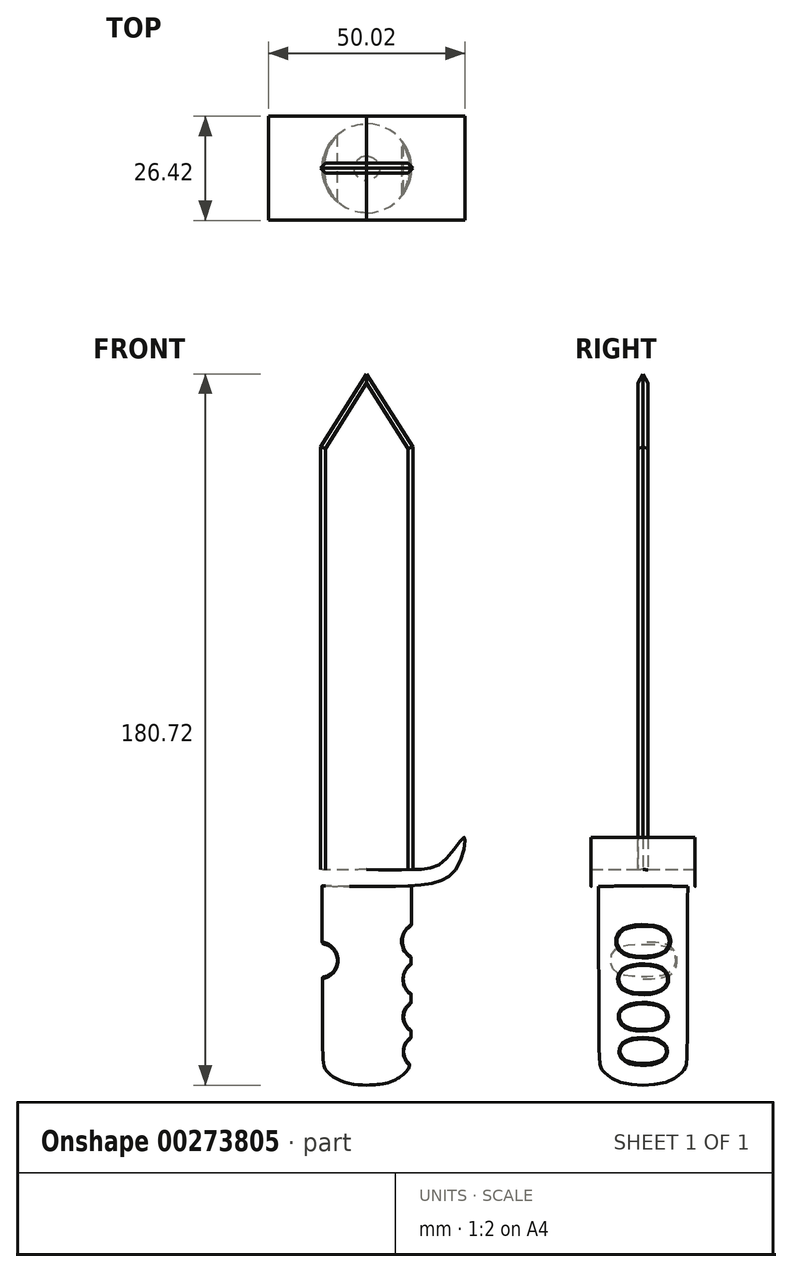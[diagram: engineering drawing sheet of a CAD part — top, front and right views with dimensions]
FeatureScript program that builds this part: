
annotation { "Feature Type Name" : "Feature", "Feature Type Description" : "" }
export const myFeature = defineFeature(function(context is Context, id is Id, definition is map)
    precondition{}
    {
        {
            var Q0;
            Q0=qCreatedBy(makeId("Front.planeOp"),FACE);
            var sketch = newSketch(context, id + "F0", { "sketchPlane" : qUnion([Q0])});
            skLineSegment(sketch, "E0", {"start": v(-11.8, -23.78) * mm, "end": v(-11.8, 52.73) * mm});
            skLineSegment(sketch, "E1", {"start": v(-11.8, 52.73) * mm, "end": v(0, 71.35) * mm});
            skLineSegment(sketch, "E2", {"start": v(0, 71.35) * mm, "end": v(0, -32.05) * mm, "construction": true});
            skLineSegment(sketch, "E3.MirrorCS", {"start": v(11.8, -23.78) * mm, "end": v(11.8, 52.73) * mm});
            skLineSegment(sketch, "E4.MirrorCS", {"start": v(11.8, 52.73) * mm, "end": v(0, 71.35) * mm});
            skLineSegment(sketch, "E5", {"start": v(-11.8, -23.78) * mm, "end": v(-11.8, -54.72) * mm});
            skLineSegment(sketch, "E6.MirrorCS", {"start": v(11.8, -23.78) * mm, "end": v(11.8, -54.72) * mm});
            skLineSegment(sketch, "E7", {"start": v(-11.8, -54.72) * mm, "end": v(11.8, -54.72) * mm});
            skSolve(sketch);
        }
        {
            var Q0;
            Q0=makeQuery(id+"F0.imprint","IMPRINT",FACE,{"disambiguationData":[TD([[makeQuery(id+"F0.imprint","IMPRINT",EDGE,{"derivedFrom":sQuery(id+"F0.wireOp",EDGE,"E0")}),-1.0]])]});
            extrude(context, id + "F1", {"entities" : qUnion([Q0]), "endBound" : BoundingType.SYMMETRIC, "depth" : 2.54 * mm});
        }
        {
            var Q0;
            Q0=makeQuery(id+"F1.opExtrude","CAP_EDGE",EDGE,{"disambiguationData":[OSD([sQuery(id+"F0.wireOp",EDGE,"E4.MirrorCS")])],"isStart":false});
            var Q1;
            Q1=makeQuery(id+"F1.opExtrude","CAP_EDGE",EDGE,{"disambiguationData":[OSD([sQuery(id+"F0.wireOp",EDGE,"E4.MirrorCS")])],"isStart":true});
            var Q2;
            Q2=makeQuery(id+"F1.opExtrude","CAP_EDGE",EDGE,{"disambiguationData":[OSD([sQuery(id+"F0.wireOp",EDGE,"E1")])],"isStart":true});
            var Q3;
            Q3=makeQuery(id+"F1.opExtrude","CAP_EDGE",EDGE,{"disambiguationData":[OSD([sQuery(id+"F0.wireOp",EDGE,"E1")])],"isStart":false});
            var Q4;
            Q4=makeQuery(id+"F1.opExtrude","CAP_EDGE",EDGE,{"disambiguationData":[OSD([sQuery(id+"F0.wireOp",EDGE,"E3.MirrorCS")])],"isStart":false});
            var Q5;
            Q5=makeQuery(id+"F1.opExtrude","CAP_EDGE",EDGE,{"disambiguationData":[OSD([sQuery(id+"F0.wireOp",EDGE,"E3.MirrorCS")])],"isStart":true});
            var Q6;
            Q6=makeQuery(id+"F1.opExtrude","CAP_EDGE",EDGE,{"disambiguationData":[OSD([sQuery(id+"F0.wireOp",EDGE,"E0")])],"isStart":true});
            var Q7;
            Q7=makeQuery(id+"F1.opExtrude","CAP_EDGE",EDGE,{"disambiguationData":[OSD([sQuery(id+"F0.wireOp",EDGE,"E0")])],"isStart":false});
            chamfer(context, id + "F2", {"entities" : qUnion([Q0, Q1, Q2, Q3, Q4, Q5, Q6, Q7]), "width" : 1.27 * mm, "tangentPropagation" : true});
        }
        {
            var Q0;
            Q0=qCreatedBy(makeId("Front.planeOp"),FACE);
            var sketch = newSketch(context, id + "F3", { "sketchPlane" : qUnion([Q0])});
            skFitSpline(sketch, "E8", {"points": [v(0, -54.6) * mm, v(-12.3, -54.6) * mm, v(-19.85, -52.22) * mm, v(-24.82, -46.4) * mm, v(-23.1, -53.73) * mm, v(-16.62, -58.05) * mm, v(0, -58.91) * mm], "startDerivative": vector(-69.64, -0.77) * mm, "endDerivative": vector(84.74, -0.03) * mm});
            skLineSegment(sketch, "E9", {"start": v(0, -67.8) * mm, "end": v(0, -37.24) * mm, "construction": true});
            skFitSpline(sketch, "E10.MirrorCS", {"points": [v(0, -54.6) * mm, v(12.3, -54.6) * mm, v(19.85, -52.22) * mm, v(24.82, -46.4) * mm, v(23.1, -53.73) * mm, v(16.62, -58.05) * mm, v(0, -58.91) * mm], "startDerivative": vector(69.64, -0.77) * mm, "endDerivative": vector(-84.74, -0.03) * mm});
            skSolve(sketch);
        }
        {
            var Q0;
            Q0=makeQuery(id+"F3.imprint","IMPRINT",FACE,{"disambiguationData":[TD([[makeQuery(id+"F3.imprint","IMPRINT",EDGE,{"derivedFrom":sQuery(id+"F3.wireOp",EDGE,"E8")}),1.0]])]});
            extrude(context, id + "F4", {"entities" : qUnion([Q0]), "operationType" : NewBodyOperationType.ADD, "endBound" : BoundingType.SYMMETRIC, "depth" : 26.42 * mm});
        }
        {
            var Q0;
            Q0=qCreatedBy(makeId("Front.planeOp"),FACE);
            var sketch = newSketch(context, id + "F5", { "sketchPlane" : qUnion([Q0])});
            skFitSpline(sketch, "E11", {"points": [v(-11.33, -58.67) * mm, v(-11.17, -101.4) * mm, v(-10.36, -105.51) * mm, v(-6.05, -108.52) * mm, v(0, -109.37) * mm], "startDerivative": vector(0.17, -110.36) * mm, "endDerivative": vector(33.33, -1.18) * mm});
            skLineSegment(sketch, "E12", {"start": v(0, -109.37) * mm, "end": v(0, -59) * mm});
            skLineSegment(sketch, "E13", {"start": v(0, -59) * mm, "end": v(-11.33, -58.67) * mm});
            skLineSegment(sketch, "E14", {"start": v(0, -109.37) * mm, "end": v(0, -59) * mm, "construction": true});
            skSolve(sketch);
        }
        {
            var Q0;
            Q0=makeQuery(id+"F5.imprint","IMPRINT",FACE,{"disambiguationData":[TD([[makeQuery(id+"F5.imprint","IMPRINT",EDGE,{"derivedFrom":sQuery(id+"F5.wireOp",EDGE,"E11")}),1.0]])]});
            var Q1;
            Q1=sQuery(id+"F5.wireOp",EDGE,"E12");
            revolve(context, id + "F6", {"operationType" : NewBodyOperationType.ADD, "entities" : qUnion([Q0]), "axis" : qUnion([Q1]), "revolveType" : RevolveType.FULL});
        }
        {
            var Q0;
            Q0=qCreatedBy(makeId("Front.planeOp"),FACE);
            var sketch = newSketch(context, id + "F7", { "sketchPlane" : qUnion([Q0])});
            skCircle(sketch, "E15", {"center": v(13.47, -72.8) * mm, "radius": 4.5 * mm});
            skCircle(sketch, "E16", {"center": v(13.57, -82.47) * mm, "radius": 4.3 * mm});
            skCircle(sketch, "E17", {"center": v(13.26, -92) * mm, "radius": 3.92 * mm});
            skCircle(sketch, "E18", {"center": v(13.33, -100.86) * mm, "radius": 3.97 * mm});
            skCircle(sketch, "E19", {"center": v(-11.64, -77.7) * mm, "radius": 4.22 * mm});
            skSolve(sketch);
        }
        {
            var Q0;
            Q0 = qSketchRegion(id + "F7", true);
            extrude(context, id + "F8", {"entities" : qUnion([Q0]), "operationType" : NewBodyOperationType.REMOVE, "endBound" : BoundingType.SYMMETRIC, "depth" : 50.8 * mm});
        }
        {
            var Q0;
            Q0=makeQuery(id+"F8.boolean.opBoolean","INTERSECT",EDGE,{"derivedFrom":[makeQuery(id+"F6.opRevolve","SWEPT_FACE",FACE,{"disambiguationData":[OSD([sQuery(id+"F5.wireOp",EDGE,"E11")])]}),makeQuery(id+"F8.opExtrude","SWEPT_FACE",FACE,{"disambiguationData":[OSD([sQuery(id+"F7.wireOp",EDGE,"E15")])]})]});
            var Q1;
            Q1=makeQuery(id+"F8.boolean.opBoolean","INTERSECT",EDGE,{"derivedFrom":[makeQuery(id+"F6.opRevolve","SWEPT_FACE",FACE,{"disambiguationData":[OSD([sQuery(id+"F5.wireOp",EDGE,"E11")])]}),makeQuery(id+"F8.opExtrude","SWEPT_FACE",FACE,{"disambiguationData":[OSD([sQuery(id+"F7.wireOp",EDGE,"E16")])]})]});
            var Q2;
            Q2=makeQuery(id+"F8.boolean.opBoolean","INTERSECT",EDGE,{"derivedFrom":[makeQuery(id+"F6.opRevolve","SWEPT_FACE",FACE,{"disambiguationData":[OSD([sQuery(id+"F5.wireOp",EDGE,"E11")])]}),makeQuery(id+"F8.opExtrude","SWEPT_FACE",FACE,{"disambiguationData":[OSD([sQuery(id+"F7.wireOp",EDGE,"E17")])]})]});
            var Q3;
            Q3=makeQuery(id+"F8.boolean.opBoolean","INTERSECT",EDGE,{"derivedFrom":[makeQuery(id+"F6.opRevolve","SWEPT_FACE",FACE,{"disambiguationData":[OSD([sQuery(id+"F5.wireOp",EDGE,"E11")])]}),makeQuery(id+"F8.opExtrude","SWEPT_FACE",FACE,{"disambiguationData":[OSD([sQuery(id+"F7.wireOp",EDGE,"E18")])]})]});
            var Q4;
            Q4=makeQuery(id+"F8.boolean.opBoolean","INTERSECT",EDGE,{"derivedFrom":[makeQuery(id+"F6.opRevolve","SWEPT_FACE",FACE,{"disambiguationData":[OSD([sQuery(id+"F5.wireOp",EDGE,"E11")])]}),makeQuery(id+"F8.opExtrude","SWEPT_FACE",FACE,{"disambiguationData":[OSD([sQuery(id+"F7.wireOp",EDGE,"E19")])]})]});
            fillet(context, id + "F9", {"entities" : qUnion([Q0, Q1, Q2, Q3, Q4]), "radius" : 0.5 * mm, "tangentPropagation" : true, "allowEdgeOverflow" : false});
        }
    });
